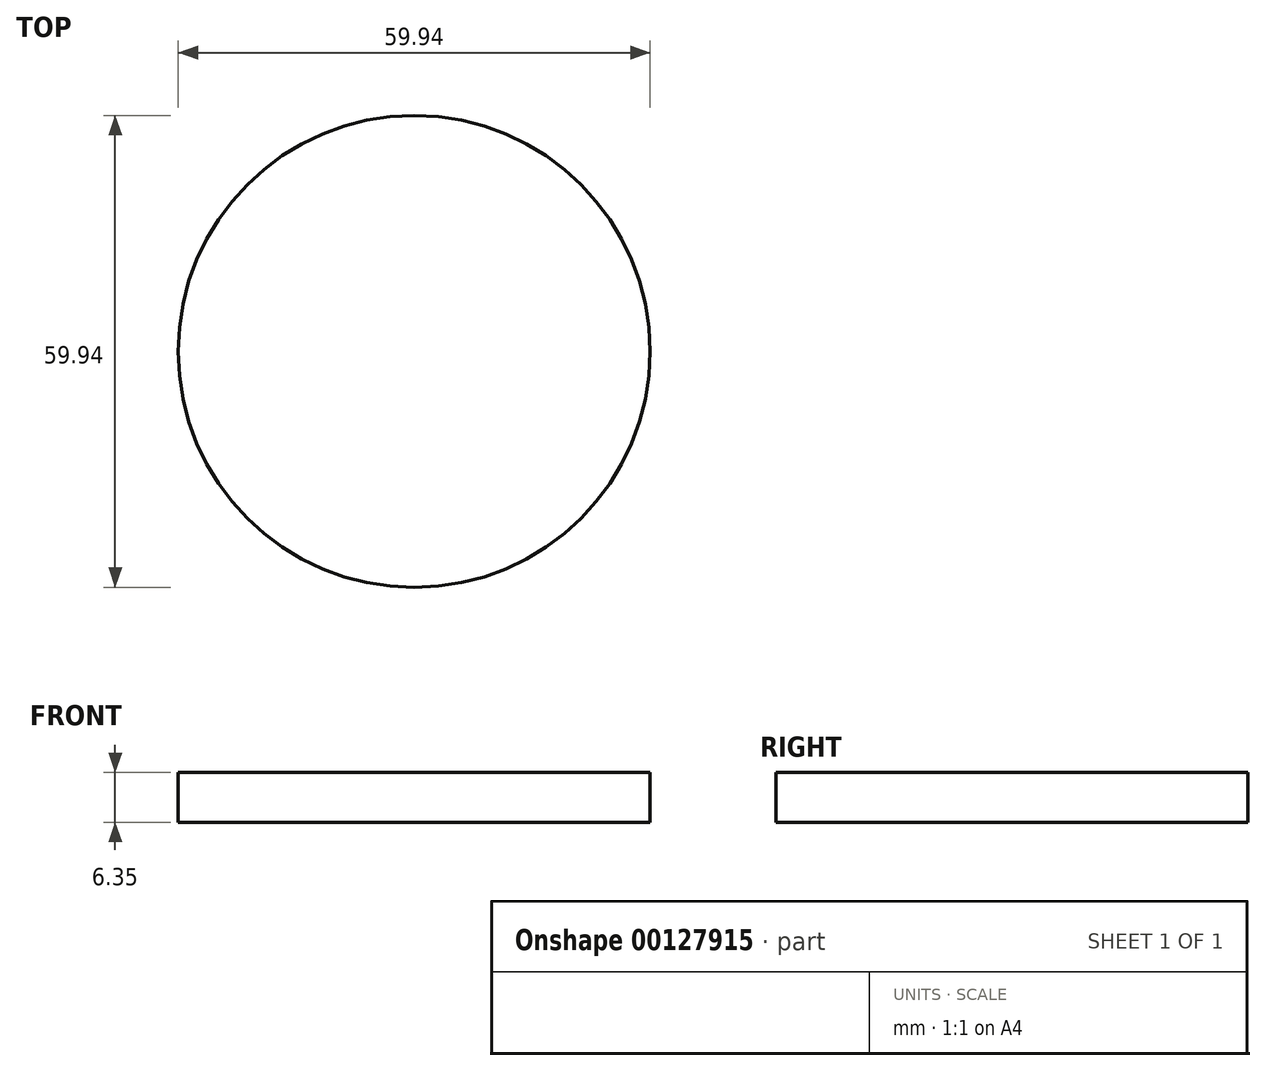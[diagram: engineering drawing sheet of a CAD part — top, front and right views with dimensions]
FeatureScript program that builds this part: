
annotation { "Feature Type Name" : "Feature", "Feature Type Description" : "" }
export const myFeature = defineFeature(function(context is Context, id is Id, definition is map)
    precondition{}
    {
        {
            var Q0;
            Q0=qCreatedBy(makeId("Top.planeOp"),FACE);
            var sketch = newSketch(context, id + "F0", { "sketchPlane" : qUnion([Q0])});
            skCircle(sketch, "E0", {"center": v(0, 0) * mm, "radius": 30.48 * mm, "construction": true});
            skCircle(sketch, "E1", {"center": v(0, 0) * mm, "radius": 29.97 * mm});
            skCircle(sketch, "E2", {"center": v(0, 0) * mm, "radius": 22.1 * mm, "construction": true});
            skCircle(sketch, "E3", {"center": v(0, 0) * mm, "radius": 18.42 * mm, "construction": true});
            skLineSegment(sketch, "E4", {"start": v(0, 18.42) * mm, "end": v(0, 30.48) * mm, "construction": true});
            skLineSegment(sketch, "E5", {"start": v(-5.12, 30.05) * mm, "end": v(-3.1, 18.16) * mm, "construction": true});
            skLineSegment(sketch, "E6", {"start": v(-3.1, 18.16) * mm, "end": v(0, 22.1) * mm, "construction": true});
            skLineSegment(sketch, "E7", {"start": v(-16.65, 24.92) * mm, "end": v(-16.93, 25.34) * mm});
            skLineSegment(sketch, "E8", {"start": v(0, 22.1) * mm, "end": v(6.1, 29.86) * mm, "construction": true});
            skLineSegment(sketch, "E9", {"start": v(5.1, 17.7) * mm, "end": v(-6.63, 21.08) * mm, "construction": true});
            skCircle(sketch, "E10", {"center": v(5.1, 17.7) * mm, "radius": 12.2 * mm});
            skLineSegment(sketch, "E11", {"start": v(-6.63, 21.08) * mm, "end": v(-8.99, 28.6) * mm, "construction": true});
            skLineSegment(sketch, "E12", {"start": v(0.53, 29.97) * mm, "end": v(0.39, 22.1) * mm, "construction": true});
            skLineSegment(sketch, "E13", {"start": v(-4.29, 29.66) * mm, "end": v(-3.16, 21.87) * mm, "construction": true});
            skLineSegment(sketch, "E14", {"start": v(-6.63, 21.08) * mm, "end": v(-4.29, 29.66) * mm, "construction": true});
            skLineSegment(sketch, "E15", {"start": v(0.39, 22.1) * mm, "end": v(-4.29, 29.66) * mm, "construction": true});
            skCircle(sketch, "E16", {"center": v(0, 0) * mm, "radius": 16.29 * mm});
            skLineSegment(sketch, "E17", {"start": v(-3.77, 15.54) * mm, "end": v(-6.76, 14.82) * mm, "construction": true});
            skLineSegment(sketch, "E18", {"start": v(-3.16, 21.87) * mm, "end": v(-3.54, 21.53) * mm});
            skLineSegment(sketch, "E19", {"start": v(-3.54, 21.53) * mm, "end": v(-12.27, 13.74) * mm, "construction": true});
            skCircle(sketch, "E20", {"center": v(-12.27, 13.74) * mm, "radius": 11.7 * mm});
            skLineSegment(sketch, "E21", {"start": v(-3.77, 15.54) * mm, "end": v(-5.69, 23.41) * mm, "construction": true});
            skLineSegment(sketch, "E22", {"start": v(-3.16, 21.87) * mm, "end": v(-6.63, 21.08) * mm, "construction": true});
            skSolve(sketch);
        }
        {
            var Q0;
            {var subQ0=sQuery(id+"F0.wireOp",EDGE,"E20");var subQ3=sQuery(id+"F0.wireOp",EDGE,"E10");var subQ4=makeQuery(id+"F0.imprint","INTERSECT",VERTEX,{"disambiguationData":[OD(1.0)],"derivedFrom":[subQ3,subQ0]});Q0=makeQuery(id+"F0.imprint","IMPRINT",FACE,{"disambiguationData":[TD([[makeQuery(id+"F0.imprint","IMPRINT",EDGE,{"disambiguationData":[TD([[subQ4,-1.0]])],"derivedFrom":subQ3}),-1.0]])]});}
            var Q1;
            {var subQ0=sQuery(id+"F0.wireOp",EDGE,"E20");var subQ3=sQuery(id+"F0.wireOp",EDGE,"E10");var subQ4=makeQuery(id+"F0.imprint","INTERSECT",VERTEX,{"disambiguationData":[OD(1.0)],"derivedFrom":[subQ3,subQ0]});Q1=makeQuery(id+"F0.imprint","IMPRINT",FACE,{"disambiguationData":[TD([[makeQuery(id+"F0.imprint","IMPRINT",EDGE,{"disambiguationData":[TD([[subQ4,-1.0]])],"derivedFrom":subQ3}),1.0]])]});}
            var Q2;
            {var subQ1=sQuery(id+"F0.wireOp",EDGE,"E16");var subQ3=sQuery(id+"F0.wireOp",EDGE,"E10");var subQ5=makeQuery(id+"F0.imprint","INTERSECT",VERTEX,{"disambiguationData":[OD(0.0)],"derivedFrom":[subQ3,subQ1]});Q2=makeQuery(id+"F0.imprint","IMPRINT",FACE,{"disambiguationData":[TD([[makeQuery(id+"F0.imprint","IMPRINT",EDGE,{"disambiguationData":[TD([[subQ5,-1.0]])],"derivedFrom":subQ3}),1.0]])]});}
            var Q3;
            {var subQ1=sQuery(id+"F0.wireOp",EDGE,"E16");var subQ3=sQuery(id+"F0.wireOp",EDGE,"E10");var subQ5=makeQuery(id+"F0.imprint","INTERSECT",VERTEX,{"disambiguationData":[OD(0.0)],"derivedFrom":[subQ3,subQ1]});Q3=makeQuery(id+"F0.imprint","IMPRINT",FACE,{"disambiguationData":[TD([[makeQuery(id+"F0.imprint","IMPRINT",EDGE,{"disambiguationData":[TD([[subQ5,-1.0]])],"derivedFrom":subQ3}),-1.0]])]});}
            var Q4;
            {var subQ0=sQuery(id+"F0.wireOp",EDGE,"E20");var subQ3=makeQuery(id+"F0.imprint","IMPRINT",VERTEX,{"derivedFrom":subQ0});Q4=makeQuery(id+"F0.imprint","IMPRINT",FACE,{"disambiguationData":[TD([[makeQuery(id+"F0.imprint","IMPRINT",EDGE,{"disambiguationData":[TD([[subQ3,-1.0]])],"derivedFrom":subQ0}),1.0]])]});}
            extrude(context, id + "F1", {"entities" : qUnion([Q0, Q1, Q2, Q3, Q4]), "depth" : 6.35 * mm});
        }
        {
            var Q0;
            Q0=makeQuery(id+"F1.opExtrude","SWEPT_BODY",BODY,{"disambiguationData":[OSD([sQuery(id+"F0.wireOp",EDGE,"E1"),sQuery(id+"F0.wireOp",EDGE,"E10"),sQuery(id+"F0.wireOp",EDGE,"E16"),sQuery(id+"F0.wireOp",EDGE,"E20")])]});
            var Q1;
            Q1=makeQuery(id+"F1.opExtrude","CAP_EDGE",EDGE,{"disambiguationData":[OSD([sQuery(id+"F0.wireOp",EDGE,"E16")])],"isStart":false});
            circularPattern(context, id + "F2", {"operationType" : NewBodyOperationType.ADD, "entities" : qUnion([Q0]), "axis" : qUnion([Q1]), "angle" : 360 * degree, "instanceCount" : 13, "equalSpace" : true, "computeTransformsWithoutBuiltin" : true});
        }
    });
